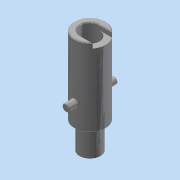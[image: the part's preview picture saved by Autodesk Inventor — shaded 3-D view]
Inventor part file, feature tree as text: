
AUTODESK INVENTOR PART (.ipt)
format: ipt  version: 2017 (Build 210142000, 142)  size: 202,752 bytes
history: native  units: mm
features: other x3, sketch x3, extrude x2, chamfer x1, mirror x1
ambient origin geometry x8: Origin, YZ Plane, XZ Plane, XY Plane, X Axis, Y Axis, Z Axis, Center Point
bodies: Body1 (feature_tree), Body2 (feature_tree), Body3 (feature_tree)
feature tree (10):
  other  "Révolution1"
  extrude  "Extrusion3"  Depth=1.0mm
  other  "Plan de construction1"
  extrude  "Extrusion4"  Depth=1.0mm
  chamfer  "Chanfrein1"  Distance=11.0mm
  mirror  "Symétrie1"
  sketch  "Esquisse3"
  sketch  "Esquisse4"
  sketch  "Esquisse5"
  other  "Projeter les arêtes coupées1"
